# Revit family: Kee_Safety_KWM21_1_5M_FREE_STANDING_MODULE_75MPH
name_source: partatom
category: Generic Models
units: mm (PartAtom-declared; Revit-internal decimal feet)

## family parameters
Can host rebar = No
Cut with Voids When Loaded = No
Host = Face
Maintain Annotation Orientation = No
Part Type = Normal
Room Calculation Point = No
Round Connector Dimension = Use Diameter
Shared = No

## types (1)
- Kee_Safety_KWM21_1_5M_FREE_STANDING_MODULE_75MPH
    Annually = Periodic inspections by a competent person are recommended by the manufacturer. In
UK/Europe these are required under Regulation 5 of the Workplace (Health, Safety &
Welfare) Regulations, the Work at Height Regulations and BS EN 365. The frequency will
depend upon the environment, location and usage but should be at least every 12 months.
Walk and visually inspect the complete installed system in relation to the clients’ general
needs. Establish if any modifications and/or additional products are required to reflect
any refurbishment requirements or additional plant & equipment which have been installed
and require access.
Check installation configuration is complete as per the original installation drawing/plan.
Ensure the system has not been modified or tampered with by unauthorised persons.
Check all Kee Walk are in place as per the original drawing. This is essential for longevity of
the roof.
Check all fixings are in place and correctly torqued.
Any galvanised components showing signs of corrosion should be wire brushed thoroughly
and galvanised spray/paint applied as appropriate. If rusted significantly, take digital
photographs and include these in the inspection report. All component and assembled
parts should be kept clean, using detergent if necessary, by wiping down with a wet cloth
or hosing with clean water, after which they should be wiped down with a dry cloth.
Where toe-boards are fitted check the brackets that support the toe-board are in place and
sufficiently torqued.
Where applicable check fixings to walls/structures including cat ladder clamps are in place
and sufficiently torqued.
If the Kee Walk becomes damaged in any, please arrange for inspection and any necessary
repair or component replacement..
    Assembly Code = KWM21
    CE Approval = Yes
    Colour = Tread Black
    Coverage Area = 1500 m²
    Default Elevation = 1219 mm
    Description = Kee Walk® System provides a safe, anti-slip, level walking surface for means of access to and across roofs. It provides a
demarcation route which protects the roof membrane from unnecessary foot traffic and potential damage. Pre-assembled
in 1,5m unit.
    Design Country = United Kingdom
    Features = Modular Rooftop walkway to EN 516
    Finish = Annodized Aluminium
    Gross Weight kg = 74
    Location of Manufacturer = Cradley Heath
    Manufacturer = Kee Safety
    Manufacturer Country = United Kingdom
    Manufacturer Website = www.keesafety.co.uk
    Material = Aluminum
    Overall Height = 167 mm
    Overall Length = 1494 mm  [stored 4.90157 ft]
    Overall Width = 620 mm  [stored 2.03412 ft]
    Product Family = KeeWalk
    Product Group = KeeWalk
    Product Literature = https://keesafety.co.uk
    Product Model Number = WW721ASSY
    Product Range = KeeWalk
    Shipping Weight kg = 74
    Width = 1590 mm

note: [stored X ft] marks values corroborated as IEEE doubles in the binary element streams (Revit-internal decimal feet)

## geometry (parser evidence)
native form markers: Sweep x8
no freeform markers — native parametric forms only
